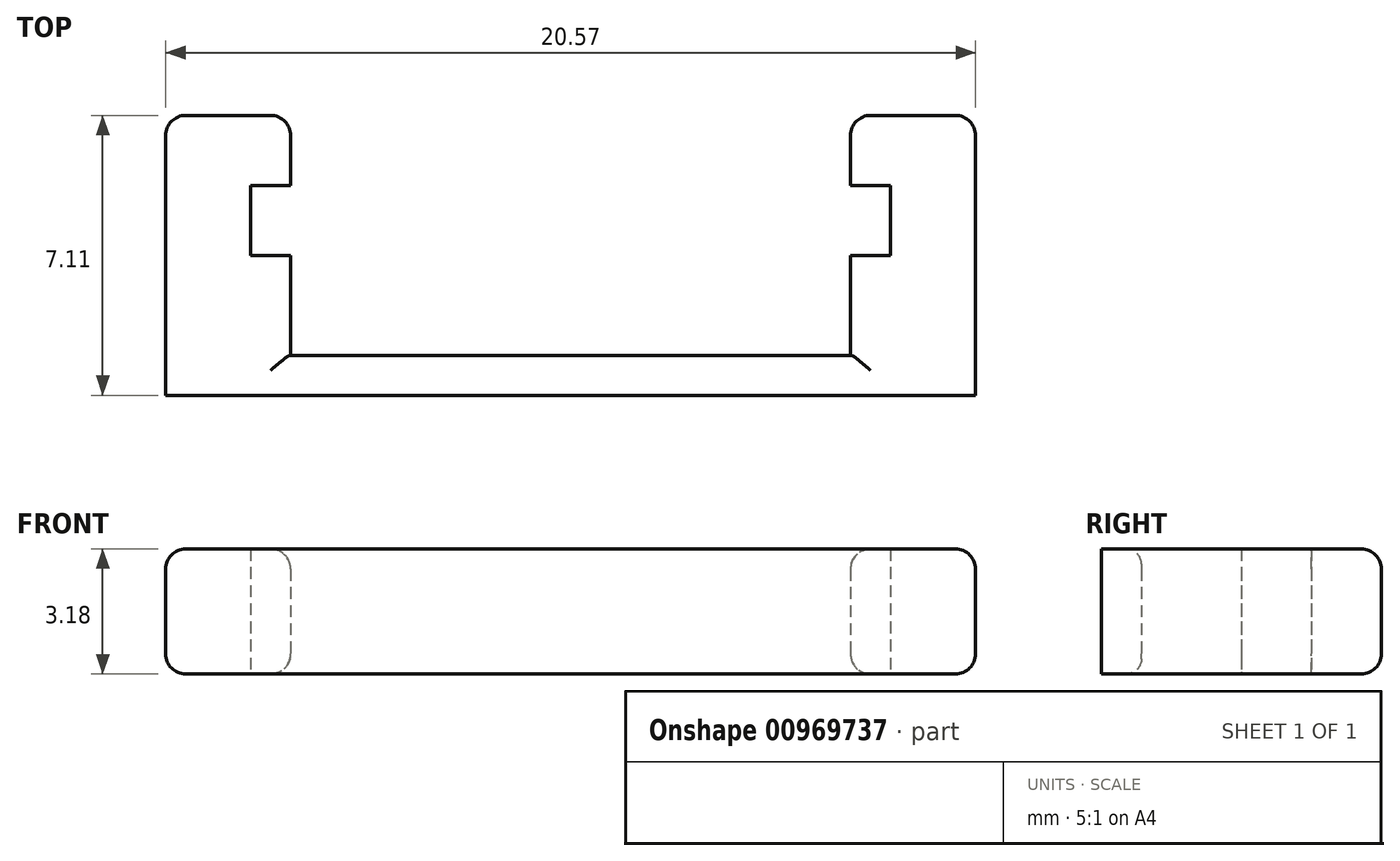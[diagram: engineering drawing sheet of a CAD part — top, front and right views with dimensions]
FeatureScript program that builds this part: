
annotation { "Feature Type Name" : "Feature", "Feature Type Description" : "" }
export const myFeature = defineFeature(function(context is Context, id is Id, definition is map)
    precondition{}
    {
        {
            var Q0;
            Q0=qCreatedBy(makeId("Top.planeOp"),FACE);
            var sketch = newSketch(context, id + "F0", { "sketchPlane" : qUnion([Q0])});
            skLineSegment(sketch, "E0.bottom", {"start": v(-14.33, 0) * mm, "end": v(6.24, 0) * mm});
            skLineSegment(sketch, "E0.top", {"start": v(-14.33, 7.11) * mm, "end": v(-11.16, 7.11) * mm});
            skLineSegment(sketch, "E0.left", {"start": v(-14.33, 0) * mm, "end": v(-14.33, 7.11) * mm});
            skLineSegment(sketch, "E0.right", {"start": v(6.24, 0) * mm, "end": v(6.24, 7.11) * mm});
            skLineSegment(sketch, "E1.top", {"start": v(-11.16, 1.02) * mm, "end": v(3.07, 1.02) * mm});
            skLineSegment(sketch, "E1.left", {"start": v(-14.33, 0) * mm, "end": v(-14.33, 1.02) * mm});
            skLineSegment(sketch, "E1.right", {"start": v(6.24, 0) * mm, "end": v(6.24, 1.02) * mm});
            skLineSegment(sketch, "E2.left", {"start": v(-14.33, 1.02) * mm, "end": v(-14.33, 7.11) * mm});
            skLineSegment(sketch, "E2.right", {"start": v(-11.16, 1.02) * mm, "end": v(-11.16, 7.11) * mm});
            skLineSegment(sketch, "E3.top", {"start": v(6.24, 7.11) * mm, "end": v(3.07, 7.11) * mm});
            skLineSegment(sketch, "E3.left", {"start": v(6.24, 1.02) * mm, "end": v(6.24, 7.11) * mm});
            skLineSegment(sketch, "E3.right", {"start": v(3.07, 1.02) * mm, "end": v(3.07, 7.11) * mm});
            skLineSegment(sketch, "E4", {"start": v(-11.16, 5.33) * mm, "end": v(-12.17, 5.33) * mm});
            skLineSegment(sketch, "E5", {"start": v(-12.17, 5.33) * mm, "end": v(-12.17, 3.56) * mm});
            skLineSegment(sketch, "E6", {"start": v(-12.17, 3.56) * mm, "end": v(-11.16, 3.56) * mm});
            skLineSegment(sketch, "E7", {"start": v(-4.04, 1.02) * mm, "end": v(-4.04, 7.11) * mm, "construction": true});
            skLineSegment(sketch, "E8.trimOffspring", {"start": v(3.07, 7.11) * mm, "end": v(6.24, 7.11) * mm});
            skLineSegment(sketch, "E9.MirrorCS", {"start": v(3.07, 5.33) * mm, "end": v(4.08, 5.33) * mm});
            skLineSegment(sketch, "E10.MirrorCS", {"start": v(4.08, 5.33) * mm, "end": v(4.08, 3.56) * mm});
            skLineSegment(sketch, "E11.MirrorCS", {"start": v(4.08, 3.56) * mm, "end": v(3.07, 3.56) * mm});
            skSolve(sketch);
        }
        {
            var Q0;
            {var subQ7=sQuery(id+"F0.wireOp",EDGE,"E0.bottom");Q0=makeQuery(id+"F0.imprint","IMPRINT",FACE,{"disambiguationData":[TD([[makeQuery(id+"F0.imprint","IMPRINT",EDGE,{"derivedFrom":subQ7}),1.0]])]});}
            extrude(context, id + "F1", {"entities" : qUnion([Q0]), "depth" : 3.17 * mm, "offsetDistance" : 25.4 * mm});
        }
        {
            var Q0;
            {var subQ0=sQuery(id+"F0.wireOp",EDGE,"E2.right");Q0=makeQuery(id+"F1.opExtrude","CAP_EDGE",EDGE,{"disambiguationData":[OSD([subQ0]),TDD([makeQuery(id+"F0.imprint","IMPRINT",EDGE,{"disambiguationData":[TD([[makeQuery(id+"F0.imprint","INTERSECT",VERTEX,{"derivedFrom":[sQuery(id+"F0.wireOp",EDGE,"E1.top"),subQ0]}),-1.0]])],"derivedFrom":subQ0})])],"isStart":false});}
            var Q1;
            {var subQ0=sQuery(id+"F0.wireOp",EDGE,"E2.right");Q1=makeQuery(id+"F1.opExtrude","CAP_EDGE",EDGE,{"disambiguationData":[OSD([subQ0]),TDD([makeQuery(id+"F0.imprint","IMPRINT",EDGE,{"disambiguationData":[TD([[makeQuery(id+"F0.imprint","INTERSECT",VERTEX,{"derivedFrom":[sQuery(id+"F0.wireOp",EDGE,"E1.top"),subQ0]}),-1.0]])],"derivedFrom":subQ0})])],"isStart":true});}
            var Q2;
            {var subQ0=sQuery(id+"F0.wireOp",EDGE,"E3.right");Q2=makeQuery(id+"F1.opExtrude","CAP_EDGE",EDGE,{"disambiguationData":[OSD([subQ0]),TDD([makeQuery(id+"F0.imprint","IMPRINT",EDGE,{"disambiguationData":[TD([[makeQuery(id+"F0.imprint","INTERSECT",VERTEX,{"derivedFrom":[sQuery(id+"F0.wireOp",EDGE,"E1.top"),subQ0]}),-1.0]])],"derivedFrom":subQ0})])],"isStart":false});}
            var Q3;
            Q3=makeQuery(id+"F1.opExtrude","CAP_EDGE",EDGE,{"disambiguationData":[OSD([sQuery(id+"F0.wireOp",EDGE,"E0.right")])],"isStart":false});
            var Q4;
            Q4=makeQuery(id+"F1.opExtrude","CAP_EDGE",EDGE,{"disambiguationData":[OSD([sQuery(id+"F0.wireOp",EDGE,"E0.right")])],"isStart":true});
            var Q5;
            Q5=makeQuery(id+"F1.opExtrude","CAP_EDGE",EDGE,{"disambiguationData":[OSD([sQuery(id+"F0.wireOp",EDGE,"E0.left")])],"isStart":false});
            var Q6;
            Q6=makeQuery(id+"F1.opExtrude","CAP_EDGE",EDGE,{"disambiguationData":[OSD([sQuery(id+"F0.wireOp",EDGE,"E0.top")])],"isStart":false});
            var Q7;
            Q7=makeQuery(id+"F1.opExtrude","SWEPT_EDGE",EDGE,{"disambiguationData":[OSD([sQuery(id+"F0.wireOp",EDGE,"E0.right"),sQuery(id+"F0.wireOp",EDGE,"E3.top")])]});
            var Q8;
            Q8=makeQuery(id+"F1.opExtrude","CAP_EDGE",EDGE,{"disambiguationData":[OSD([sQuery(id+"F0.wireOp",EDGE,"E3.top")])],"isStart":false});
            var Q9;
            Q9=makeQuery(id+"F1.opExtrude","CAP_EDGE",EDGE,{"disambiguationData":[OSD([sQuery(id+"F0.wireOp",EDGE,"E3.top")])],"isStart":true});
            var Q10;
            Q10=makeQuery(id+"F1.opExtrude","SWEPT_EDGE",EDGE,{"disambiguationData":[OSD([sQuery(id+"F0.wireOp",EDGE,"E3.top"),sQuery(id+"F0.wireOp",EDGE,"E3.right")])]});
            var Q11;
            Q11=makeQuery(id+"F1.opExtrude","SWEPT_EDGE",EDGE,{"disambiguationData":[OSD([sQuery(id+"F0.wireOp",EDGE,"E0.top"),sQuery(id+"F0.wireOp",EDGE,"E2.right")])]});
            var Q12;
            Q12=makeQuery(id+"F1.opExtrude","CAP_EDGE",EDGE,{"disambiguationData":[OSD([sQuery(id+"F0.wireOp",EDGE,"E0.top")])],"isStart":true});
            var Q13;
            Q13=makeQuery(id+"F1.opExtrude","SWEPT_EDGE",EDGE,{"disambiguationData":[OSD([sQuery(id+"F0.wireOp",EDGE,"E0.top"),sQuery(id+"F0.wireOp",EDGE,"E0.left")])]});
            var Q14;
            {var subQ0=sQuery(id+"F0.wireOp",EDGE,"E2.right");Q14=makeQuery(id+"F1.opExtrude","CAP_EDGE",EDGE,{"disambiguationData":[OSD([subQ0]),TDD([makeQuery(id+"F0.imprint","IMPRINT",EDGE,{"disambiguationData":[TD([[makeQuery(id+"F0.imprint","INTERSECT",VERTEX,{"derivedFrom":[sQuery(id+"F0.wireOp",EDGE,"E0.top"),subQ0]}),1.0]])],"derivedFrom":subQ0})])],"isStart":false});}
            var Q15;
            {var subQ0=sQuery(id+"F0.wireOp",EDGE,"E2.right");Q15=makeQuery(id+"F1.opExtrude","CAP_EDGE",EDGE,{"disambiguationData":[OSD([subQ0]),TDD([makeQuery(id+"F0.imprint","IMPRINT",EDGE,{"disambiguationData":[TD([[makeQuery(id+"F0.imprint","INTERSECT",VERTEX,{"derivedFrom":[sQuery(id+"F0.wireOp",EDGE,"E0.top"),subQ0]}),1.0]])],"derivedFrom":subQ0})])],"isStart":true});}
            var Q16;
            {var subQ0=sQuery(id+"F0.wireOp",EDGE,"E3.right");Q16=makeQuery(id+"F1.opExtrude","CAP_EDGE",EDGE,{"disambiguationData":[OSD([subQ0]),TDD([makeQuery(id+"F0.imprint","IMPRINT",EDGE,{"disambiguationData":[TD([[makeQuery(id+"F0.imprint","INTERSECT",VERTEX,{"derivedFrom":[sQuery(id+"F0.wireOp",EDGE,"E3.top"),subQ0]}),1.0]])],"derivedFrom":subQ0})])],"isStart":false});}
            var Q17;
            {var subQ0=sQuery(id+"F0.wireOp",EDGE,"E3.right");Q17=makeQuery(id+"F1.opExtrude","CAP_EDGE",EDGE,{"disambiguationData":[OSD([subQ0]),TDD([makeQuery(id+"F0.imprint","IMPRINT",EDGE,{"disambiguationData":[TD([[makeQuery(id+"F0.imprint","INTERSECT",VERTEX,{"derivedFrom":[sQuery(id+"F0.wireOp",EDGE,"E3.top"),subQ0]}),1.0]])],"derivedFrom":subQ0})])],"isStart":true});}
            var Q18;
            {var subQ0=sQuery(id+"F0.wireOp",EDGE,"E3.right");Q18=makeQuery(id+"F1.opExtrude","CAP_EDGE",EDGE,{"disambiguationData":[OSD([subQ0]),TDD([makeQuery(id+"F0.imprint","IMPRINT",EDGE,{"disambiguationData":[TD([[makeQuery(id+"F0.imprint","INTERSECT",VERTEX,{"derivedFrom":[sQuery(id+"F0.wireOp",EDGE,"E1.top"),subQ0]}),-1.0]])],"derivedFrom":subQ0})])],"isStart":true});}
            var Q19;
            Q19=makeQuery(id+"F1.opExtrude","CAP_EDGE",EDGE,{"disambiguationData":[OSD([sQuery(id+"F0.wireOp",EDGE,"E0.left")])],"isStart":true});
            fillet(context, id + "F2", {"entities" : qUnion([Q0, Q1, Q2, Q3, Q4, Q5, Q6, Q7, Q8, Q9, Q10, Q11, Q12, Q13, Q14, Q15, Q16, Q17, Q18, Q19]), "radius" : 0.5 * mm, "tangentPropagation" : true, "allowEdgeOverflow" : false});
        }
        {
            var Q0;
            Q0=makeQuery(id+"F1.opExtrude","CAP_EDGE",EDGE,{"disambiguationData":[OSD([sQuery(id+"F0.wireOp",EDGE,"E1.top")])],"isStart":true});
            var Q1;
            Q1=makeQuery(id+"F1.opExtrude","CAP_EDGE",EDGE,{"disambiguationData":[OSD([sQuery(id+"F0.wireOp",EDGE,"E1.top")])],"isStart":false});
            fillet(context, id + "F3", {"entities" : qUnion([Q0, Q1]), "radius" : 0.38 * mm, "tangentPropagation" : true, "allowEdgeOverflow" : false});
        }
    });
